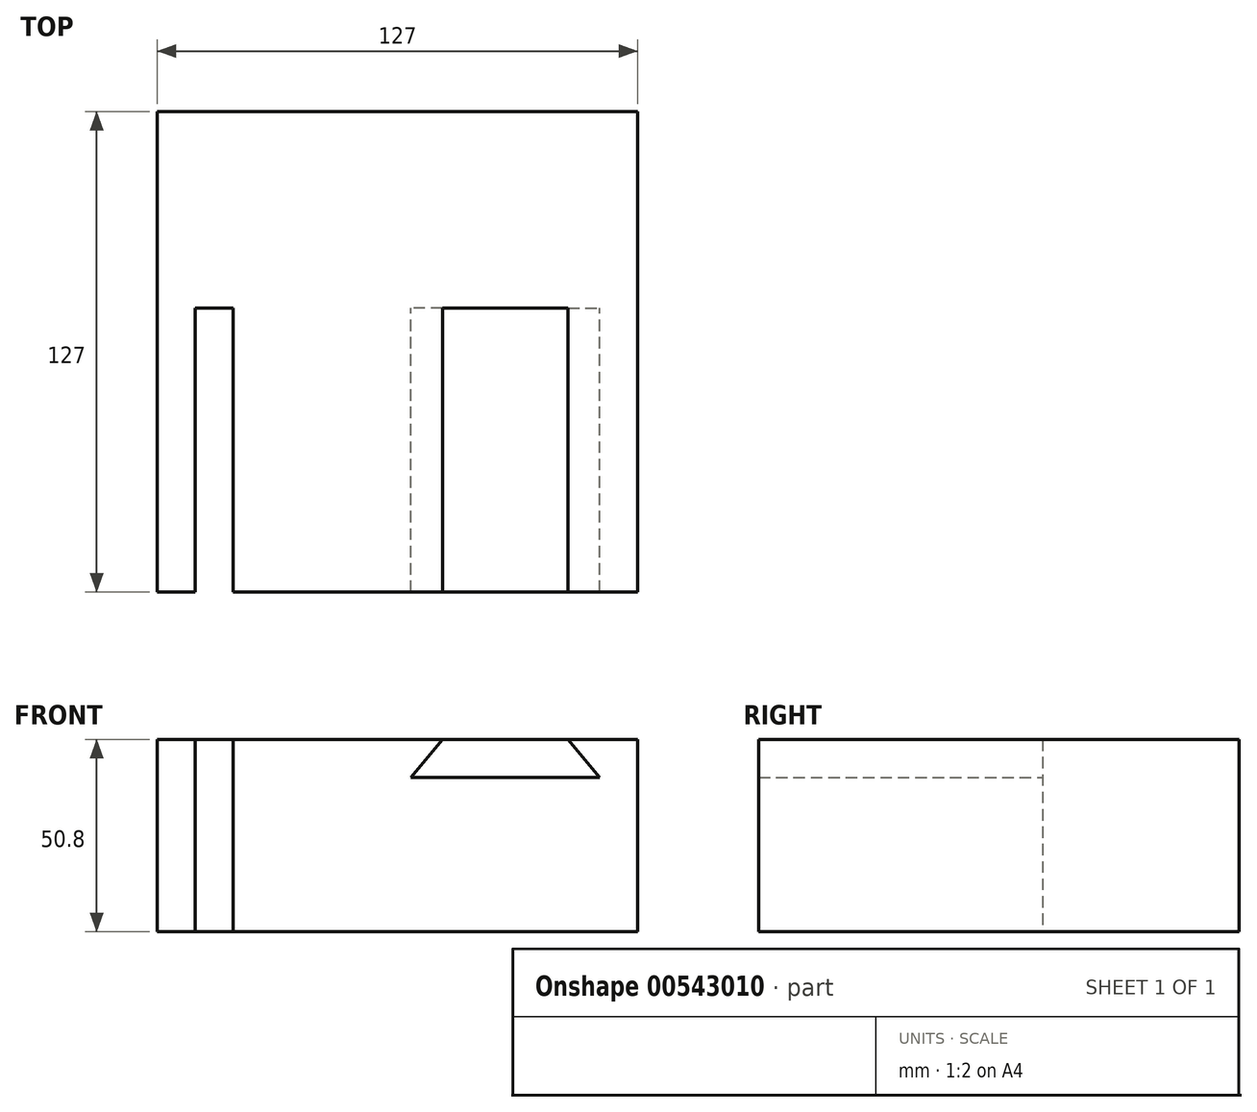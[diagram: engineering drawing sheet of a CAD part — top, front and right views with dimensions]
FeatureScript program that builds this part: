
annotation { "Feature Type Name" : "Feature", "Feature Type Description" : "" }
export const myFeature = defineFeature(function(context is Context, id is Id, definition is map)
    precondition{}
    {
        {
            var Q0;
            Q0=qCreatedBy(makeId("Front.planeOp"),FACE);
            var sketch = newSketch(context, id + "F0", { "sketchPlane" : qUnion([Q0])});
            skLineSegment(sketch, "E0.bottom", {"start": v(63.5, -25.4) * mm, "end": v(-63.5, -25.4) * mm});
            skLineSegment(sketch, "E0.top", {"start": v(63.5, 25.4) * mm, "end": v(-63.5, 25.4) * mm});
            skLineSegment(sketch, "E0.left", {"start": v(63.5, -25.4) * mm, "end": v(63.5, 25.4) * mm});
            skLineSegment(sketch, "E0.right", {"start": v(-63.5, -25.4) * mm, "end": v(-63.5, 25.4) * mm});
            skPoint(sketch, "E0.middle", {"position": v(0, 0) * mm});
            skSolve(sketch);
        }
        {
            var Q0;
            Q0=makeQuery(id+"F0.imprint","IMPRINT",FACE,{"disambiguationData":[TD([[makeQuery(id+"F0.imprint","IMPRINT",EDGE,{"derivedFrom":sQuery(id+"F0.wireOp",EDGE,"E0.bottom")}),-1.0]])]});
            extrude(context, id + "F1", {"entities" : qUnion([Q0]), "endBound" : BoundingType.SYMMETRIC, "depth" : 127 * mm, "offsetDistance" : 25 * mm});
        }
        {
            var Q0;
            Q0=makeQuery(id+"F1.opExtrude","CAP_FACE",FACE,{"disambiguationData":[OSD([sQuery(id+"F0.wireOp",EDGE,"E0.bottom"),sQuery(id+"F0.wireOp",EDGE,"E0.top"),sQuery(id+"F0.wireOp",EDGE,"E0.left"),sQuery(id+"F0.wireOp",EDGE,"E0.right")])],"isStart":false});
            var sketch = newSketch(context, id + "F2", { "sketchPlane" : qUnion([Q0])});
            skLineSegment(sketch, "E1", {"start": v(-53.5, 25.4) * mm, "end": v(-53.5, -25.4) * mm});
            skLineSegment(sketch, "E2", {"start": v(-53.5, -25.4) * mm, "end": v(-43.5, -25.4) * mm});
            skLineSegment(sketch, "E3", {"start": v(-43.5, -25.4) * mm, "end": v(-43.5, 25.4) * mm});
            skLineSegment(sketch, "E4", {"start": v(-43.5, 25.4) * mm, "end": v(-53.5, 25.4) * mm});
            skLineSegment(sketch, "E5", {"start": v(11.9, 25.4) * mm, "end": v(3.5, 15.4) * mm});
            skLineSegment(sketch, "E6", {"start": v(3.5, 15.4) * mm, "end": v(53.5, 15.4) * mm});
            skLineSegment(sketch, "E7", {"start": v(53.5, 15.4) * mm, "end": v(45.1, 25.4) * mm});
            skLineSegment(sketch, "E8", {"start": v(45.1, 25.4) * mm, "end": v(11.9, 25.4) * mm});
            skSolve(sketch);
        }
        {
            var Q0;
            Q0 = qSketchRegion(id + "F2", true);
            extrude(context, id + "F3", {"entities" : qUnion([Q0]), "operationType" : NewBodyOperationType.REMOVE, "endBound" : BoundingType.SYMMETRIC, "depth" : 150 * mm, "offsetDistance" : 25 * mm});
        }
    });
